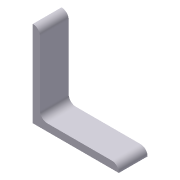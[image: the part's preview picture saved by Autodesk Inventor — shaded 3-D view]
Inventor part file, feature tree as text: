
AUTODESK INVENTOR PART (.ipt)
format: ipt  version: 2012 (Build 160160000, 160)  size: 73,216 bytes
history: native  units: in
note: dims shown in document units (in); Inventor stores cm internally (conversion verified against a paired STEP export)
features: extrude x1, sketch x1
ambient origin geometry x8: Origin, YZ Plane, XZ Plane, XY Plane, X Axis, Y Axis, Z Axis, Center Point
bodies: Solid1 (feature_tree)
feature tree (2):
  extrude  "Extrusion1"  Depth=0.25in
  sketch  "Sketch1"  dims[d0=0.24in d1=0.25in d2=3.0in d3=0.25in d4=1.0in d5=0.0in]
